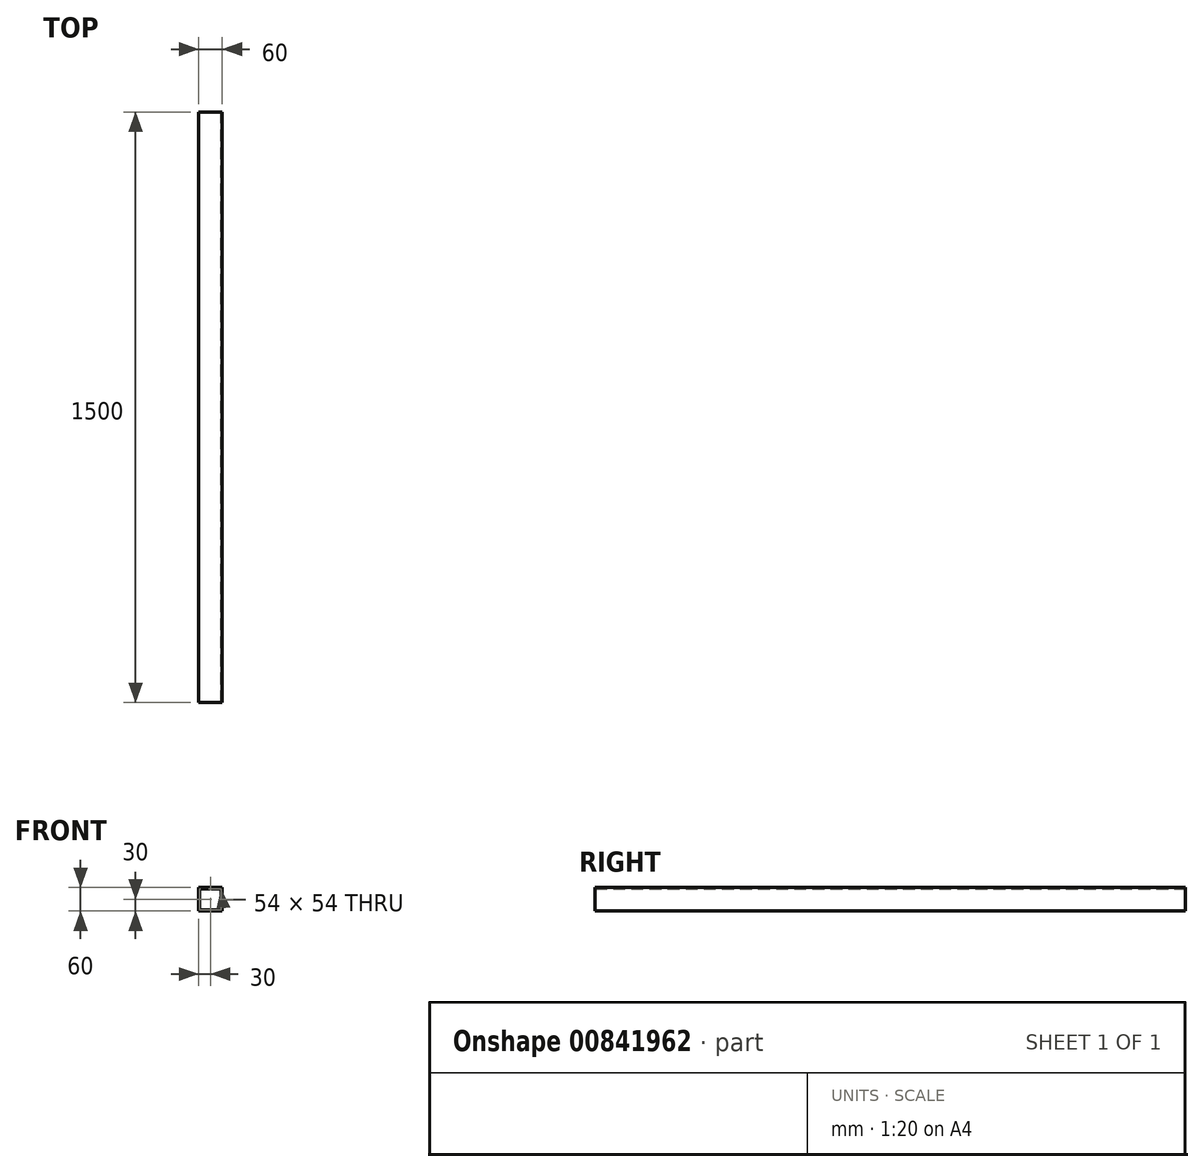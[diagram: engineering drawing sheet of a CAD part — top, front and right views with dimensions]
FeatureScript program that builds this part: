
annotation { "Feature Type Name" : "Feature", "Feature Type Description" : "" }
export const myFeature = defineFeature(function(context is Context, id is Id, definition is map)
    precondition{}
    {
        {
            var Q0;
            Q0=qCreatedBy(makeId("Front.planeOp"),FACE);
            var sketch = newSketch(context, id + "F0", { "sketchPlane" : qUnion([Q0])});
            skLineSegment(sketch, "E0.bottom", {"start": v(-30, 30) * mm, "end": v(30, 30) * mm});
            skLineSegment(sketch, "E0.top", {"start": v(-30, -30) * mm, "end": v(30, -30) * mm});
            skLineSegment(sketch, "E0.left", {"start": v(-30, 30) * mm, "end": v(-30, -30) * mm});
            skLineSegment(sketch, "E0.right", {"start": v(30, 30) * mm, "end": v(30, -30) * mm});
            skLineSegment(sketch, "E1.0", {"start": v(-27, 27) * mm, "end": v(-27, -27) * mm});
            skLineSegment(sketch, "E1.1", {"start": v(-27, 27) * mm, "end": v(27, 27) * mm});
            skLineSegment(sketch, "E1.2", {"start": v(27, 27) * mm, "end": v(27, -27) * mm});
            skLineSegment(sketch, "E1.3", {"start": v(-27, -27) * mm, "end": v(27, -27) * mm});
            skSolve(sketch);
        }
        {
            var Q0;
            Q0=makeQuery(id+"F0.imprint","IMPRINT",FACE,{"disambiguationData":[TD([[makeQuery(id+"F0.imprint","IMPRINT",EDGE,{"derivedFrom":sQuery(id+"F0.wireOp",EDGE,"E0.bottom")}),-1.0]])]});
            extrude(context, id + "F1", {"entities" : qUnion([Q0]), "endBound" : BoundingType.SYMMETRIC, "depth" : 1500 * mm, "offsetDistance" : 25 * mm});
        }
    });
